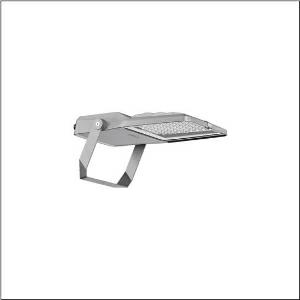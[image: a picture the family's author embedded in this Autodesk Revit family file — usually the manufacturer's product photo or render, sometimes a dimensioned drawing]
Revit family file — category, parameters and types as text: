
# Revit family: floodlight_fl_21_iq_mini___pl33t_5xa7771b4f1a_48a0
name_source: partatom
category: Lighting Fixtures
units: mm (PartAtom-declared; Revit-internal decimal feet)

## family parameters
Cut with Voids When Loaded = No
Host = Face
Light Source = No
Part Type = Normal
Room Calculation Point = No
Round Connector Dimension = Use Diameter
Shared = No

## types (1)
- --- (1 x LED, 6420 lm, 45.5 W, 4000K)
    Apparent Load = 46 VA
    CIE Flux Codes = 26 75 99 100 100
    Color Rendering = 70
    Color Temperature = 4000K
    Default Elevation = 1800 mm
    Description = Floodlight FL 21 iQ mini, floodlight, primary light control with lens, of PMMA, primary optical cover: protective disc, of toughened safety glass, transparent, light distribution: PL33T, light emission: direct distribution, installation type: surface-mounted, lamps: LED, High Power LED, rated values: 6.420lm | 45,5W | 141,1lm/W (begin service life); end service life: 6.420lm | 48W; at 50% lumin. flux: 3.210lm | 21,5W | 149,3lm/W, colour temperature: 4000K, colour rendering: CRI > 70, light colour: 740, light setting 1 begin service life: 100% | 6.420lm | 45,5W | 141,1lm/W | 4.000K, light setting 1 end service life: 48W, further light settings possible, control: Auto-Match, Temp-Guard, Lumen-Switch, Night-Set, Smart-Wire, Light-Fading, Desk-Remote (wireless, voltage-free reading and setting of iQ features in the workshop via application-optimized NFC function/RFID function), optimised constant luminous flux control (CLO 2.0), pre-setting: linear dimming characteristic, with terminal, 6-pole, mains connection: 220..240V, AC, 50/60Hz, luminaire housing, of diecast aluminium, powder-coated, SITECO metallic grey (DB 702S), corrosivity category C5 mid according to DIN EN ISO 12944suitable for swimming poolschlorine-resistant, sealing non-destructively replaceable, mounting bracket, of steel, galvanised, powder-coated, SITECO metallic grey (DB 702S), protection rating (complete): IP66, insulation class (complete): insulation class II (safety insulation), certification: CE, ENEC, VDE, protection symbol: D, impact resistance: IK08, permissible operating ambient temperature: -40..+40°C, permissible operating ambient temperature for outdoor applications: -40..+50°C, standard: DIN EN 12944, LABS conformity tested according to VDMA 24364:2018-05, packaging unit: 1 piece

Light Distribution: PL33T
    Height = 70 mm
    Lamp = 1 x LED
    Lamp Light Flux = 6420 lm
    Lamp Power = 45.5 W
    Lamp count = 1
    Length = 485 mm
    Luminous efficacy = 141 lm/W
    Manufacturer = Siteco
    ModVariant = No
    Model = 5XA7771B4F1A
    Mounting Place = Wall
    Mounting Type = Surface mounted
    Number of Poles = 1
    OnlyDefault = Yes
    Power Factor = 1
    Product Name = Floodlight FL 21 iQ mini | PL33T
    Product group = floodlight | wall mounted
    ProductGroupID = 2002
    Protection Class = Protection class II
    Protection Degree = IP 66
    RLX_Detail_Level = 1
    RLX_Emergency_Light_Flux = 0 lm
    RLX_Emergency_Type = 0
    RLX_Emergency_Type_DB = No
    RlxData = <blob elided: 96297 chars, md5=a0f9810e>
    Socket = socket
    Standby Power = 0 W
    System Light Flux = 6420 lm
    System Power = 46 W
    Type Comments = factory setting: luminous flux: 100 % | dim-lin: 254 | 463 mA
    Type Image = l_1006845.jpg
    URL = http://relux.com
    VarID = @adj_149743
    Voltage = 0 V
    Weight = 0.00 kg
    Width = 337 mm

## geometry (parser evidence)
native form markers: Blend x4, Sweep x13
no freeform markers — native parametric forms only
